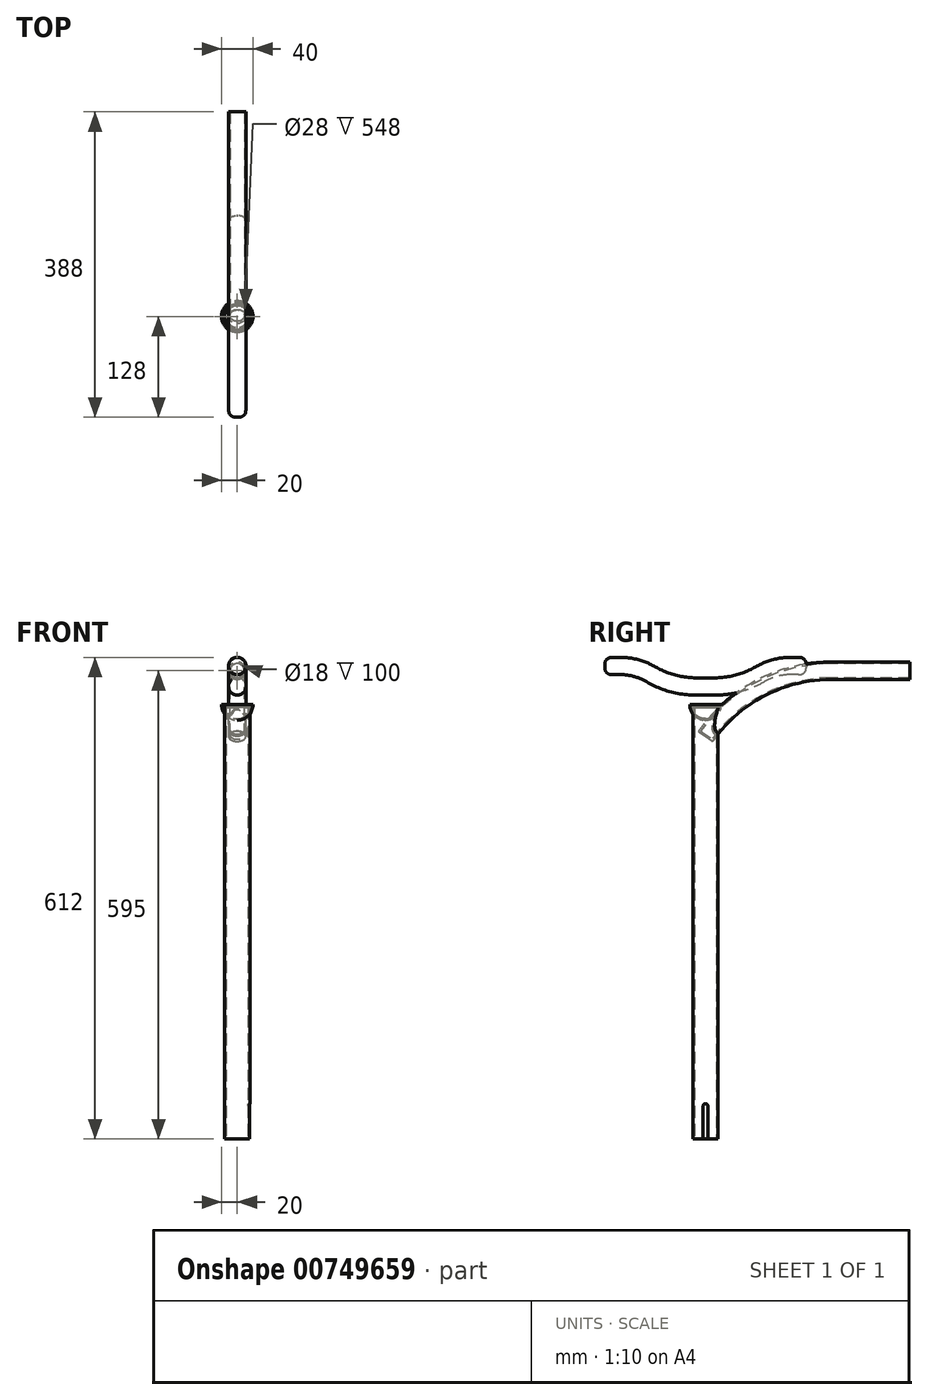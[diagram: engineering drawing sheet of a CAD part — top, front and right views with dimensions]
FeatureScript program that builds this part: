
annotation { "Feature Type Name" : "Feature", "Feature Type Description" : "" }
export const myFeature = defineFeature(function(context is Context, id is Id, definition is map)
    precondition{}
    {
        {
            var Q0;
            Q0=qCreatedBy(makeId("Top.planeOp"),FACE);
            var sketch = newSketch(context, id + "F0", { "sketchPlane" : qUnion([Q0])});
            skCircle(sketch, "E0", {"center": v(0, 0) * mm, "radius": 16 * mm});
            skSolve(sketch);
        }
        {
            var Q0;
            Q0=qSketchRegion(id+"F0",true);
            extrude(context, id + "F1", {"entities" : qUnion([Q0]), "depth" : 550 * mm, "offsetDistance" : 25 * mm});
        }
        {
            var Q0;
            Q0=makeQuery(id+"F1.opExtrude","CAP_FACE",FACE,{"disambiguationData":[OSD([sQuery(id+"F0.wireOp",EDGE,"E0")])],"isStart":true});
            shell(context, id + "F2", {"entities" : qUnion([Q0]), "thickness" : 2 * mm});
        }
        {
            var Q0;
            Q0=qCreatedBy(makeId("Right.planeOp"),FACE);
            var sketch = newSketch(context, id + "F3", { "sketchPlane" : qUnion([Q0])});
            skLineSegment(sketch, "E1.bottom", {"start": v(-3, 0) * mm, "end": v(3, 0) * mm});
            skLineSegment(sketch, "E1.top", {"start": v(0, 45) * mm, "end": v(0, 45) * mm});
            skLineSegment(sketch, "E1.left", {"start": v(-3, 0) * mm, "end": v(-3, 42) * mm});
            skLineSegment(sketch, "E1.right", {"start": v(3, 0) * mm, "end": v(3, 42) * mm});
            skPoint(sketch, "E2.visualSharp", {"position": v(-3, 45) * mm});
            skArc(sketch, "E2.filletArc", {"start": v(0, 45) * mm, "mid": v(-2.12, 44.12) * mm, "end": v(-3, 42) * mm});
            skPoint(sketch, "E3.visualSharp", {"position": v(3, 45) * mm});
            skArc(sketch, "E3.filletArc", {"start": v(3, 42) * mm, "mid": v(2.12, 44.12) * mm, "end": v(0, 45) * mm});
            skSolve(sketch);
        }
        {
            var Q0;
            Q0=qSketchRegion(id+"F3",true);
            extrude(context, id + "F4", {"entities" : qUnion([Q0]), "operationType" : NewBodyOperationType.REMOVE, "endBound" : BoundingType.THROUGH_ALL, "depth" : 25 * mm, "offsetDistance" : 25 * mm});
        }
        {
            var Q0;
            Q0=qCreatedBy(makeId("Right.planeOp"),FACE);
            var sketch = newSketch(context, id + "F5", { "sketchPlane" : qUnion([Q0])});
            skArc(sketch, "E4", {"start": v(160, 595) * mm, "mid": v(69.75, 572.86) * mm, "end": v(0, 511.47) * mm});
            skLineSegment(sketch, "E5", {"start": v(160, 595) * mm, "end": v(260, 595) * mm});
            skSolve(sketch);
        }
        {
            var Q0;
            Q0=sQuery(id+"F5.wireOp",VERTEX,"E5.end");
            var Q1;
            Q1=qCreatedBy(makeId("Front.planeOp"),FACE);
            cPlane(context, id + "F6", {"entities" : qUnion([Q0, Q1]), "cplaneType" : CPlaneType.PLANE_POINT, "offset" : 25 * mm, "width" : 150 * mm, "height" : 150 * mm});
        }
        {
            var Q0;
            Q0=qCreatedBy(id+"F6.planeOp",FACE);
            var sketch = newSketch(context, id + "F7", { "sketchPlane" : qUnion([Q0])});
            skCircle(sketch, "E6", {"center": v(0, 595) * mm, "radius": 11 * mm});
            skSolve(sketch);
        }
        {
            var Q0;
            Q0=qSketchRegion(id+"F7",true);
            var Q1;
            Q1=qConstructionFilter(qBodyType(qCreatedBy(id+"F5",EDGE),BodyType.WIRE),ConstructionObject.NO);
            sweep(context, id + "F8", {"operationType" : NewBodyOperationType.ADD, "profiles" : qUnion([Q0]), "path" : qUnion([Q1])});
        }
        {
            var Q0;
            Q0=makeQuery(id+"F8.opSweep","CAP_FACE",FACE,{"disambiguationData":[OSD([sQuery(id+"F5.wireOp",VERTEX,"E5.end"),sQuery(id+"F7.wireOp",EDGE,"E6")])],"isStart":true});
            shell(context, id + "F9", {"entities" : qUnion([Q0]), "thickness" : 2 * mm});
        }
        {
            var Q0;
            Q0=qCreatedBy(makeId("Right.planeOp"),FACE);
            var sketch = newSketch(context, id + "F10", { "sketchPlane" : qUnion([Q0])});
            skLineSegment(sketch, "E7", {"start": v(0, 575) * mm, "end": v(-12.5, 575) * mm});
            skLineSegment(sketch, "E8", {"start": v(0, 0) * mm, "end": v(0, 575) * mm, "construction": true});
            skArc(sketch, "E9", {"start": v(-69.28, 590.46) * mm, "mid": v(-41.92, 578.93) * mm, "end": v(-12.5, 575) * mm});
            skArc(sketch, "E10", {"start": v(-69.28, 590.46) * mm, "mid": v(-87.93, 598.32) * mm, "end": v(-108, 601) * mm});
            skLineSegment(sketch, "E11", {"start": v(-108, 601) * mm, "end": v(-128, 601) * mm});
            skLineSegment(sketch, "E12.MirrorCS", {"start": v(108, 601) * mm, "end": v(128, 601) * mm});
            skArc(sketch, "E13.MirrorCS", {"start": v(69.28, 590.46) * mm, "mid": v(87.93, 598.32) * mm, "end": v(108, 601) * mm});
            skArc(sketch, "E14.MirrorCS", {"start": v(69.28, 590.46) * mm, "mid": v(41.92, 578.93) * mm, "end": v(12.5, 575) * mm});
            skLineSegment(sketch, "E15.MirrorCS", {"start": v(0, 575) * mm, "end": v(12.5, 575) * mm});
            skSolve(sketch);
        }
        {
            var Q0;
            Q0=sQuery(id+"F10.wireOp",VERTEX,"E12.MirrorCS.end");
            var Q1;
            Q1=qCreatedBy(id+"F6.planeOp",FACE);
            cPlane(context, id + "F11", {"entities" : qUnion([Q0, Q1]), "cplaneType" : CPlaneType.PLANE_POINT, "offset" : 25 * mm, "width" : 150 * mm, "height" : 150 * mm});
        }
        {
            var Q0;
            Q0=qCreatedBy(id+"F11.planeOp",FACE);
            var sketch = newSketch(context, id + "F12", { "sketchPlane" : qUnion([Q0])});
            skCircle(sketch, "E16", {"center": v(0, 601) * mm, "radius": 11 * mm});
            skSolve(sketch);
        }
        {
            var Q0;
            Q0=qSketchRegion(id+"F12",true);
            var Q1;
            Q1=qConstructionFilter(qBodyType(qCreatedBy(id+"F10",EDGE),BodyType.WIRE),ConstructionObject.NO);
            sweep(context, id + "F13", {"profiles" : qUnion([Q0]), "path" : qUnion([Q1])});
        }
        {
            var Q0;
            Q0=makeQuery(id+"F13.opSweep","CAP_EDGE",EDGE,{"disambiguationData":[OSD([sQuery(id+"F10.wireOp",VERTEX,"E11.end"),sQuery(id+"F12.wireOp",EDGE,"E16")])],"isStart":false});
            var Q1;
            Q1=makeQuery(id+"F13.opSweep","CAP_EDGE",EDGE,{"disambiguationData":[OSD([sQuery(id+"F10.wireOp",VERTEX,"E12.MirrorCS.end"),sQuery(id+"F12.wireOp",EDGE,"E16")])],"isStart":true});
            fillet(context, id + "F14", {"entities" : qUnion([Q0, Q1]), "radius" : 10 * mm, "tangentPropagation" : true, "rho" : 0.5, "crossSection" : FilletCrossSection.CONIC, "allowEdgeOverflow" : false});
        }
        {
            var Q0;
            Q0=qCreatedBy(makeId("Right.planeOp"),FACE);
            var sketch = newSketch(context, id + "F15", { "sketchPlane" : qUnion([Q0])});
            skArc(sketch, "E17", {"start": v(-20, 552) * mm, "mid": v(-14.14, 537.86) * mm, "end": v(0, 532) * mm});
            skLineSegment(sketch, "E18", {"start": v(0, 552) * mm, "end": v(0, 532) * mm});
            skLineSegment(sketch, "E19", {"start": v(0, 552) * mm, "end": v(-20, 552) * mm});
            skSolve(sketch);
        }
        {
            var Q0;
            Q0=qSketchRegion(id+"F15",true);
            var Q1;
            Q1=sQuery(id+"F15.wireOp",EDGE,"E18");
            revolve(context, id + "F16", {"entities" : qUnion([Q0]), "axis" : qUnion([Q1]), "revolveType" : RevolveType.FULL});
        }
        {
            var Q0;
            Q0=makeQuery(id+"F16.opRevolve","SWEPT_FACE",FACE,{"disambiguationData":[OSD([sQuery(id+"F15.wireOp",EDGE,"E19")])]});
            shell(context, id + "F17", {"entities" : qUnion([Q0]), "thickness" : 2 * mm});
        }
    });
